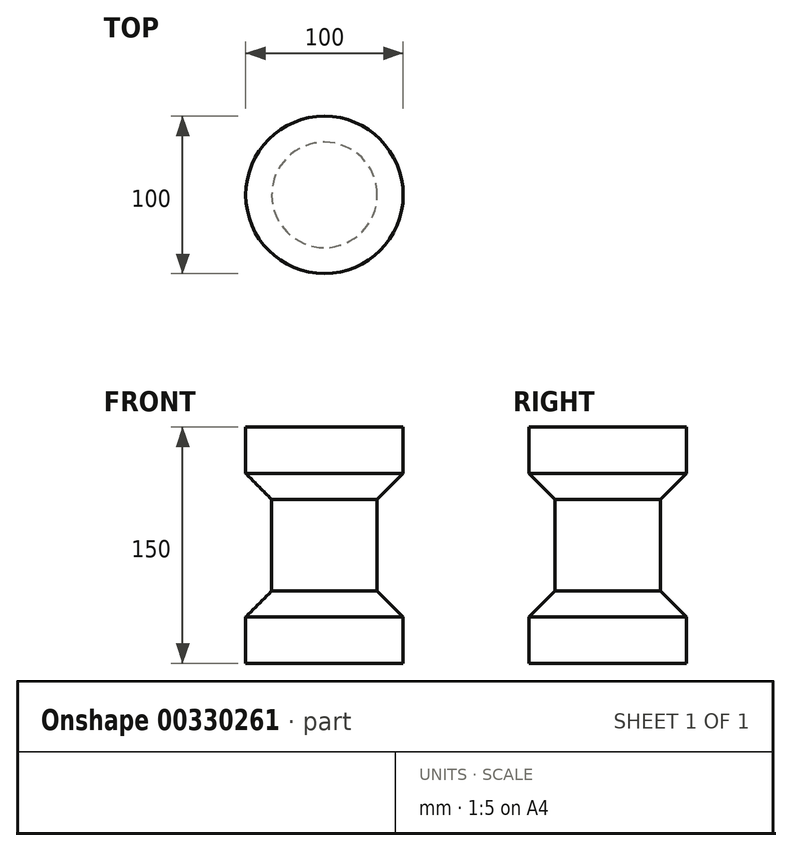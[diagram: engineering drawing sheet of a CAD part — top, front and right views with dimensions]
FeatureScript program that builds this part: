
annotation { "Feature Type Name" : "Feature", "Feature Type Description" : "" }
export const myFeature = defineFeature(function(context is Context, id is Id, definition is map)
    precondition{}
    {
        {
            var Q0;
            Q0=qCreatedBy(makeId("Front.planeOp"),FACE);
            var sketch = newSketch(context, id + "F0", { "sketchPlane" : qUnion([Q0])});
            skLineSegment(sketch, "E0", {"start": v(0, 0) * mm, "end": v(0, 102.83) * mm});
            skLineSegment(sketch, "E1", {"start": v(0, 102.83) * mm, "end": v(-50, 102.83) * mm});
            skLineSegment(sketch, "E2", {"start": v(-50, 102.83) * mm, "end": v(-50, 73.36) * mm});
            skLineSegment(sketch, "E3", {"start": v(-50, 73.36) * mm, "end": v(-33.5, 56.85) * mm});
            skLineSegment(sketch, "E4", {"start": v(-33.5, 56.85) * mm, "end": v(-33.5, -1.2) * mm});
            skLineSegment(sketch, "E5", {"start": v(-33.5, -1.2) * mm, "end": v(-50, -17.7) * mm});
            skLineSegment(sketch, "E6", {"start": v(-50, -17.7) * mm, "end": v(-50, -47.17) * mm});
            skLineSegment(sketch, "E7", {"start": v(-50, -47.17) * mm, "end": v(0, -47.17) * mm});
            skLineSegment(sketch, "E8", {"start": v(0, -47.17) * mm, "end": v(0, 0) * mm});
            skSolve(sketch);
        }
        {
            var Q0;
            Q0=makeQuery(id+"F0.imprint","IMPRINT",FACE,{"disambiguationData":[TD([[makeQuery(id+"F0.imprint","IMPRINT",EDGE,{"derivedFrom":sQuery(id+"F0.wireOp",EDGE,"E0")}),1.0]])]});
            var Q1;
            Q1=sQuery(id+"F0.wireOp",EDGE,"E0");
            revolve(context, id + "F1", {"entities" : qUnion([Q0]), "axis" : qUnion([Q1]), "revolveType" : RevolveType.FULL});
        }
    });
